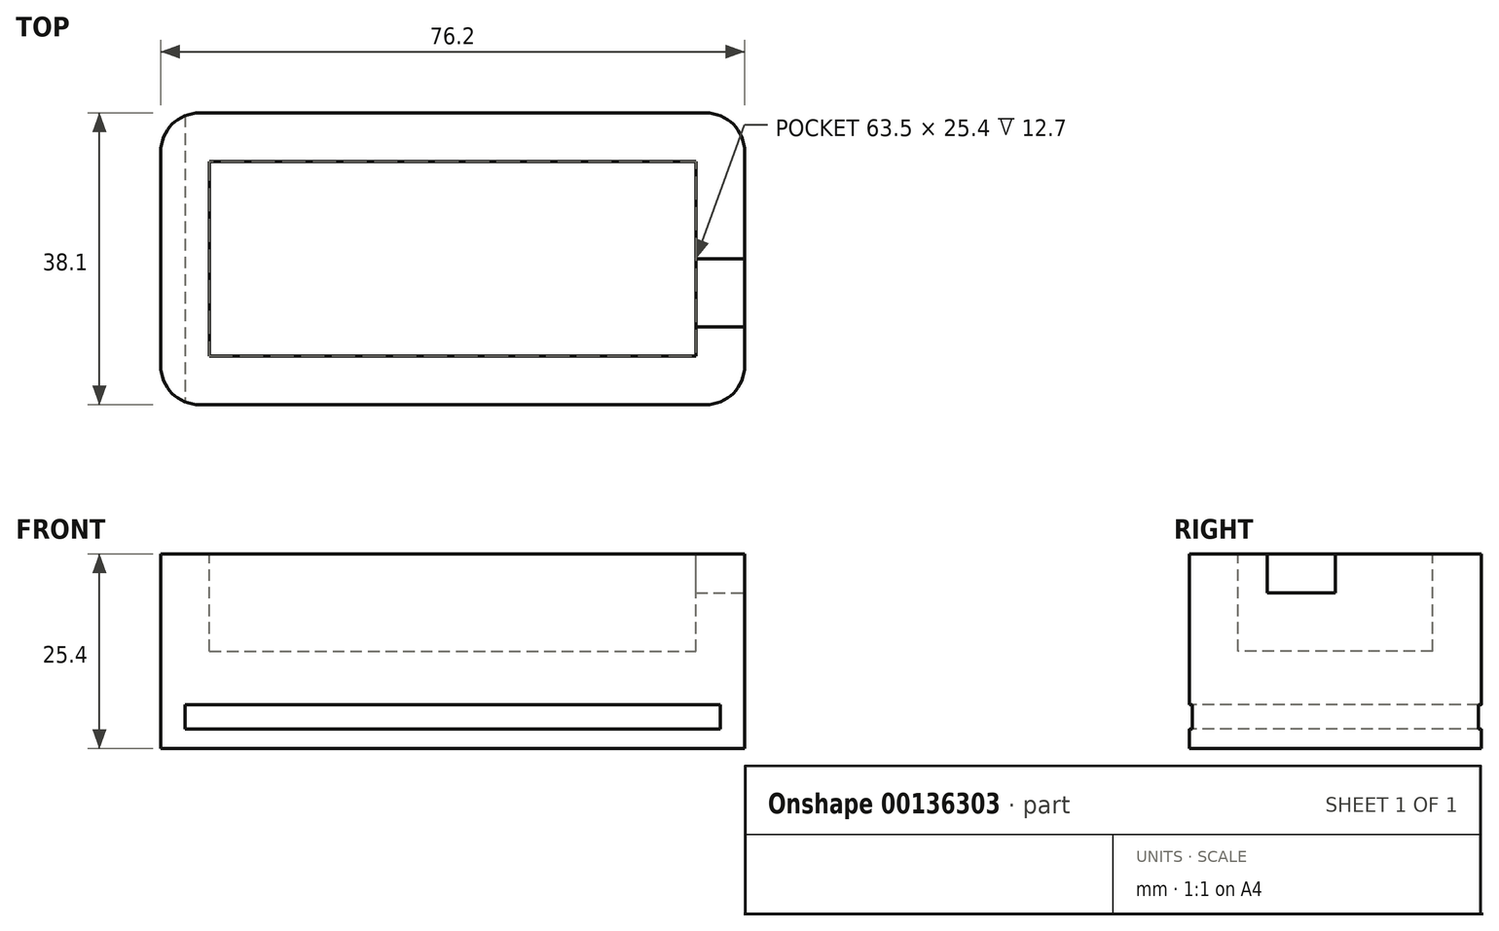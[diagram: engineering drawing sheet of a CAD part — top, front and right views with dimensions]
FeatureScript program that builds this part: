
annotation { "Feature Type Name" : "Feature", "Feature Type Description" : "" }
export const myFeature = defineFeature(function(context is Context, id is Id, definition is map)
    precondition{}
    {
        {
            var Q0;
            Q0=qCreatedBy(makeId("Top.planeOp"),FACE);
            var sketch = newSketch(context, id + "F0", { "sketchPlane" : qUnion([Q0])});
            skLineSegment(sketch, "E0.bottom", {"start": v(-31.37, 10.28) * mm, "end": v(44.83, 10.28) * mm});
            skLineSegment(sketch, "E0.top", {"start": v(-31.37, -27.82) * mm, "end": v(44.83, -27.82) * mm});
            skLineSegment(sketch, "E0.left", {"start": v(-31.37, 10.28) * mm, "end": v(-31.37, -27.82) * mm});
            skLineSegment(sketch, "E0.right", {"start": v(44.83, 10.28) * mm, "end": v(44.83, -27.82) * mm});
            skSolve(sketch);
        }
        {
            var Q0;
            Q0=makeQuery(id+"F0.imprint","IMPRINT",FACE,{"disambiguationData":[TD([[makeQuery(id+"F0.imprint","IMPRINT",EDGE,{"derivedFrom":sQuery(id+"F0.wireOp",EDGE,"E0.bottom")}),-1.0]])]});
            extrude(context, id + "F1", {"entities" : qUnion([Q0]), "depth" : 25.4 * mm});
        }
        {
            var Q0;
            Q0=makeQuery(id+"F1.opExtrude","SWEPT_FACE",FACE,{"disambiguationData":[OSD([sQuery(id+"F0.wireOp",EDGE,"E0.top")])]});
            var sketch = newSketch(context, id + "F2", { "sketchPlane" : qUnion([Q0])});
            skLineSegment(sketch, "E1.bottom", {"start": v(-28.2, 5.71) * mm, "end": v(41.65, 5.71) * mm});
            skLineSegment(sketch, "E1.top", {"start": v(-28.2, 2.54) * mm, "end": v(41.65, 2.54) * mm});
            skLineSegment(sketch, "E1.left", {"start": v(-28.2, 5.71) * mm, "end": v(-28.2, 2.54) * mm});
            skLineSegment(sketch, "E1.right", {"start": v(41.65, 5.72) * mm, "end": v(41.65, 2.54) * mm});
            skSolve(sketch);
        }
        {
            var Q0;
            Q0=makeQuery(id+"F2.imprint","IMPRINT",FACE,{"disambiguationData":[TD([[makeQuery(id+"F2.imprint","IMPRINT",EDGE,{"derivedFrom":sQuery(id+"F2.wireOp",EDGE,"E1.bottom")}),-1.0]])]});
            extrude(context, id + "F3", {"entities" : qUnion([Q0]), "operationType" : NewBodyOperationType.REMOVE, "endBound" : BoundingType.THROUGH_ALL, "oppositeDirection" : true, "depth" : 25.4 * mm});
        }
        {
            var Q0;
            Q0=makeQuery(id+"F1.opExtrude","CAP_FACE",FACE,{"disambiguationData":[OSD([sQuery(id+"F0.wireOp",EDGE,"E0.bottom"),sQuery(id+"F0.wireOp",EDGE,"E0.top"),sQuery(id+"F0.wireOp",EDGE,"E0.left"),sQuery(id+"F0.wireOp",EDGE,"E0.right")])],"isStart":false});
            var sketch = newSketch(context, id + "F4", { "sketchPlane" : qUnion([Q0])});
            skLineSegment(sketch, "E2.bottom", {"start": v(-25.02, 3.93) * mm, "end": v(38.48, 3.93) * mm});
            skLineSegment(sketch, "E2.top", {"start": v(-25.02, -21.47) * mm, "end": v(38.48, -21.47) * mm});
            skLineSegment(sketch, "E2.left", {"start": v(-25.02, 3.93) * mm, "end": v(-25.02, -21.47) * mm});
            skLineSegment(sketch, "E2.right", {"start": v(38.48, 3.93) * mm, "end": v(38.48, -21.47) * mm});
            skSolve(sketch);
        }
        {
            var Q0;
            Q0=makeQuery(id+"F4.imprint","IMPRINT",FACE,{"disambiguationData":[TD([[makeQuery(id+"F4.imprint","IMPRINT",EDGE,{"derivedFrom":sQuery(id+"F4.wireOp",EDGE,"E2.bottom")}),-1.0]])]});
            extrude(context, id + "F5", {"entities" : qUnion([Q0]), "operationType" : NewBodyOperationType.REMOVE, "oppositeDirection" : true, "depth" : 12.7 * mm});
        }
        {
            var Q0;
            Q0=makeQuery(id+"F1.opExtrude","CAP_FACE",FACE,{"disambiguationData":[OSD([sQuery(id+"F0.wireOp",EDGE,"E0.bottom"),sQuery(id+"F0.wireOp",EDGE,"E0.top"),sQuery(id+"F0.wireOp",EDGE,"E0.left"),sQuery(id+"F0.wireOp",EDGE,"E0.right")])],"isStart":false});
            var sketch = newSketch(context, id + "F6", { "sketchPlane" : qUnion([Q0])});
            skLineSegment(sketch, "E3.bottom", {"start": v(38.48, -8.77) * mm, "end": v(44.83, -8.77) * mm});
            skLineSegment(sketch, "E3.top", {"start": v(38.48, -17.66) * mm, "end": v(44.83, -17.66) * mm});
            skLineSegment(sketch, "E3.left", {"start": v(38.48, -8.77) * mm, "end": v(38.48, -17.66) * mm});
            skLineSegment(sketch, "E3.right", {"start": v(44.83, -8.77) * mm, "end": v(44.83, -17.66) * mm});
            skSolve(sketch);
        }
        {
            var Q0;
            Q0=makeQuery(id+"F6.imprint","IMPRINT",FACE,{"disambiguationData":[TD([[makeQuery(id+"F6.imprint","IMPRINT",EDGE,{"derivedFrom":sQuery(id+"F6.wireOp",EDGE,"E3.bottom")}),-1.0]])]});
            extrude(context, id + "F7", {"entities" : qUnion([Q0]), "operationType" : NewBodyOperationType.REMOVE, "oppositeDirection" : true, "depth" : 5.08 * mm});
        }
        {
            var Q0;
            Q0=makeQuery(id+"F1.opExtrude","SWEPT_EDGE",EDGE,{"disambiguationData":[OSD([sQuery(id+"F0.wireOp",EDGE,"E0.bottom"),sQuery(id+"F0.wireOp",EDGE,"E0.right")])]});
            var Q1;
            Q1=makeQuery(id+"F1.opExtrude","SWEPT_EDGE",EDGE,{"disambiguationData":[OSD([sQuery(id+"F0.wireOp",EDGE,"E0.bottom"),sQuery(id+"F0.wireOp",EDGE,"E0.left")])]});
            var Q2;
            Q2=makeQuery(id+"F1.opExtrude","SWEPT_EDGE",EDGE,{"disambiguationData":[OSD([sQuery(id+"F0.wireOp",EDGE,"E0.top"),sQuery(id+"F0.wireOp",EDGE,"E0.right")])]});
            var Q3;
            Q3=makeQuery(id+"F1.opExtrude","SWEPT_EDGE",EDGE,{"disambiguationData":[OSD([sQuery(id+"F0.wireOp",EDGE,"E0.top"),sQuery(id+"F0.wireOp",EDGE,"E0.left")])]});
            fillet(context, id + "F8", {"entities" : qUnion([Q0, Q1, Q2, Q3]), "radius" : 5.08 * mm, "tangentPropagation" : true, "allowEdgeOverflow" : false});
        }
    });
